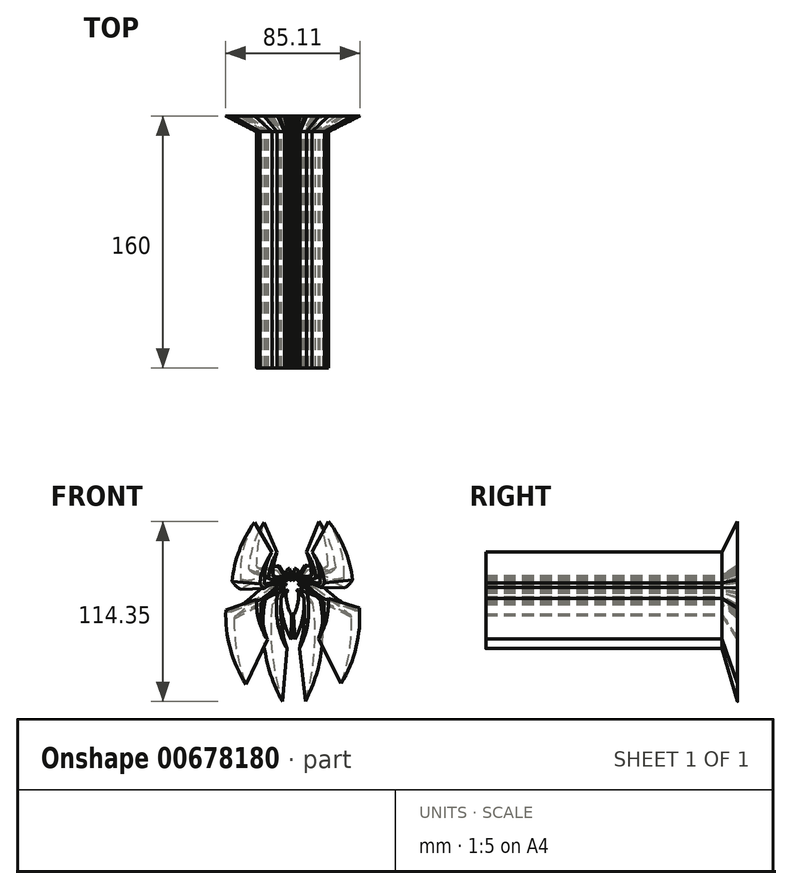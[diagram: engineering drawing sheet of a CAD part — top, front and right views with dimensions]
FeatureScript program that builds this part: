
annotation { "Feature Type Name" : "Feature", "Feature Type Description" : "" }
export const myFeature = defineFeature(function(context is Context, id is Id, definition is map)
    precondition{}
    {
        {
            var Q0;
            Q0=qCreatedBy(makeId("Front.planeOp"),FACE);
            var sketch = newSketch(context, id + "F0", { "sketchPlane" : qUnion([Q0])});
            skArc(sketch, "E0", {"start": v(-12.95, 21.82) * mm, "mid": v(-18.14, 12.28) * mm, "end": v(-20.61, 1.7) * mm});
            skArc(sketch, "E1", {"start": v(-7.35, 2.72) * mm, "mid": v(-12.76, 1.42) * mm, "end": v(-17.74, -1.05) * mm});
            skLineSegment(sketch, "E2", {"start": v(-7.35, 2.72) * mm, "end": v(-4.17, 1.94) * mm});
            skLineSegment(sketch, "E3", {"start": v(-4.17, 0.92) * mm, "end": v(-8.94, 0.99) * mm});
            skLineSegment(sketch, "E4", {"start": v(-20.96, -8.77) * mm, "end": v(-22.05, -8.77) * mm});
            skLineSegment(sketch, "E5", {"start": v(-22.05, -8.77) * mm, "end": v(-22.72, -8.06) * mm});
            skArc(sketch, "E6", {"start": v(-22.72, -8.06) * mm, "mid": v(-21.2, -21.34) * mm, "end": v(-15.81, -33.57) * mm});
            skArc(sketch, "E7", {"start": v(-19.94, -11.2) * mm, "mid": v(-18.92, -22.58) * mm, "end": v(-15.81, -33.57) * mm});
            skArc(sketch, "E8", {"start": v(-9.25, -4.09) * mm, "mid": v(-6.79, -2.87) * mm, "end": v(-5, -0.78) * mm});
            skArc(sketch, "E9", {"start": v(-9.25, -4.09) * mm, "mid": v(-9.38, -22.21) * mm, "end": v(-3.45, -39.34) * mm});
            skArc(sketch, "E10", {"start": v(-6.96, -6.37) * mm, "mid": v(-6.9, -23.04) * mm, "end": v(-3.45, -39.34) * mm});
            skArc(sketch, "E11", {"start": v(-3.45, -2.1) * mm, "mid": v(-5.56, -3.95) * mm, "end": v(-6.96, -6.37) * mm});
            skArc(sketch, "E12", {"start": v(-2.87, -2.74) * mm, "mid": v(-3.03, -2.3) * mm, "end": v(-3.45, -2.1) * mm});
            skArc(sketch, "E13", {"start": v(-2.87, -2.74) * mm, "mid": v(-3.6, -3.27) * mm, "end": v(-3.96, -4.09) * mm});
            skArc(sketch, "E14", {"start": v(-3.96, -4.09) * mm, "mid": v(-3.09, -11.38) * mm, "end": v(-0.42, -18.22) * mm});
            skArc(sketch, "E15", {"start": v(0.24, -17.46) * mm, "mid": v(-0.3, -17.65) * mm, "end": v(-0.42, -18.22) * mm});
            skArc(sketch, "E16", {"start": v(-4.17, 0.92) * mm, "mid": v(-3.96, 1.43) * mm, "end": v(-4.17, 1.94) * mm});
            skArc(sketch, "E17", {"start": v(-20.96, -8.77) * mm, "mid": v(-14.65, -4.26) * mm, "end": v(-8.94, 0.99) * mm});
            skArc(sketch, "E18", {"start": v(-5, -0.78) * mm, "mid": v(-6.44, -0.47) * mm, "end": v(-7.87, -0.78) * mm});
            skArc(sketch, "E19", {"start": v(-19.36, -10.12) * mm, "mid": v(-13.61, -5.46) * mm, "end": v(-7.87, -0.78) * mm});
            skArc(sketch, "E20", {"start": v(-19.36, -10.12) * mm, "mid": v(-19.82, -10.57) * mm, "end": v(-19.94, -11.2) * mm});
            skArc(sketch, "E21", {"start": v(-20.61, 1.7) * mm, "mid": v(-19.32, 0.17) * mm, "end": v(-17.74, -1.05) * mm});
            skArc(sketch, "E22", {"start": v(-12.95, 21.82) * mm, "mid": v(-16.8, 12.49) * mm, "end": v(-17.74, 2.44) * mm});
            skArc(sketch, "E23", {"start": v(-17.74, 2.44) * mm, "mid": v(-17.57, 1.78) * mm, "end": v(-16.9, 1.7) * mm});
            skArc(sketch, "E24", {"start": v(-16.9, 1.7) * mm, "mid": v(-12.62, 2.7) * mm, "end": v(-8.54, 4.31) * mm});
            skArc(sketch, "E25", {"start": v(-6.8, 4.31) * mm, "mid": v(-7.67, 4.47) * mm, "end": v(-8.54, 4.31) * mm});
            skArc(sketch, "E26", {"start": v(-6.8, 4.31) * mm, "mid": v(-5.62, 3.5) * mm, "end": v(-4.33, 2.85) * mm});
            skArc(sketch, "E27", {"start": v(-4.33, 2.85) * mm, "mid": v(-3.97, 2.98) * mm, "end": v(-3.9, 3.36) * mm});
            skArc(sketch, "E28", {"start": v(-3.9, 3.36) * mm, "mid": v(-4.45, 4.49) * mm, "end": v(-5.37, 5.34) * mm});
            skArc(sketch, "E29", {"start": v(-5.37, 5.34) * mm, "mid": v(-8.87, 5.53) * mm, "end": v(-12.34, 5.02) * mm});
            skArc(sketch, "E30", {"start": v(-12.96, 4.31) * mm, "mid": v(-12.61, 4.63) * mm, "end": v(-12.34, 5.02) * mm});
            skArc(sketch, "E31", {"start": v(-15, 5.99) * mm, "mid": v(-14.07, 5.04) * mm, "end": v(-12.96, 4.31) * mm});
            skArc(sketch, "E32", {"start": v(-9.71, 21.82) * mm, "mid": v(-13.3, 14.22) * mm, "end": v(-15, 5.99) * mm});
            skArc(sketch, "E33", {"start": v(-9.71, 21.82) * mm, "mid": v(-11.7, 14.5) * mm, "end": v(-12.34, 6.95) * mm});
            skArc(sketch, "E34", {"start": v(-12.34, 6.95) * mm, "mid": v(-12.26, 6.64) * mm, "end": v(-12.02, 6.43) * mm});
            skArc(sketch, "E35", {"start": v(-12.02, 6.43) * mm, "mid": v(-8.49, 6.3) * mm, "end": v(-5.02, 6.95) * mm});
            skArc(sketch, "E36", {"start": v(-4.51, 6.95) * mm, "mid": v(-4.76, 7.03) * mm, "end": v(-5.02, 6.95) * mm});
            skArc(sketch, "E37", {"start": v(-4.51, 6.95) * mm, "mid": v(-3.87, 5.55) * mm, "end": v(-2.67, 4.6) * mm});
            skArc(sketch, "E38", {"start": v(-2.67, 4.6) * mm, "mid": v(-2.4, 4.75) * mm, "end": v(-2.22, 5) * mm});
            skArc(sketch, "E39", {"start": v(-0.95, 6.13) * mm, "mid": v(-1.72, 5.7) * mm, "end": v(-2.22, 5) * mm});
            skArc(sketch, "E40", {"start": v(-1.4, 5) * mm, "mid": v(-1.1, 5.53) * mm, "end": v(-0.95, 6.13) * mm});
            skArc(sketch, "E41", {"start": v(-1.4, 5) * mm, "mid": v(-1.52, 4.91) * mm, "end": v(-1.56, 4.78) * mm});
            skArc(sketch, "E42", {"start": v(-1.56, 4.78) * mm, "mid": v(-1.55, 4.46) * mm, "end": v(-1.4, 4.18) * mm});
            skArc(sketch, "E43", {"start": v(-1.4, 4.18) * mm, "mid": v(-1.14, 4.04) * mm, "end": v(-0.87, 4.18) * mm});
            skArc(sketch, "E44", {"start": v(-0.4, 5) * mm, "mid": v(-0.75, 4.65) * mm, "end": v(-0.87, 4.18) * mm});
            skArc(sketch, "E45", {"start": v(0, 4.18) * mm, "mid": v(-0.11, 4.63) * mm, "end": v(-0.4, 5) * mm});
            skArc(sketch, "E46", {"start": v(0, 4.18) * mm, "mid": v(0.17, 4.06) * mm, "end": v(0.36, 3.98) * mm});
            skArc(sketch, "E47.MirrorCS", {"start": v(9.35, -3.85) * mm, "mid": v(9.94, -21.96) * mm, "end": v(4.46, -39.24) * mm});
            skArc(sketch, "E48.MirrorCS", {"start": v(7.12, -6.2) * mm, "mid": v(7.48, -22.85) * mm, "end": v(4.46, -39.24) * mm});
            skArc(sketch, "E49.MirrorCS", {"start": v(0.2, -17.46) * mm, "mid": v(0.76, -17.63) * mm, "end": v(0.88, -18.2) * mm});
            skArc(sketch, "E50.MirrorCS", {"start": v(4.07, -3.99) * mm, "mid": v(3.38, -11.3) * mm, "end": v(0.88, -18.2) * mm});
            skArc(sketch, "E51.MirrorCS", {"start": v(2.94, -2.67) * mm, "mid": v(3.68, -3.17) * mm, "end": v(4.07, -3.99) * mm});
            skArc(sketch, "E52.MirrorCS", {"start": v(2.94, -2.67) * mm, "mid": v(3.1, -2.22) * mm, "end": v(3.5, -2) * mm});
            skArc(sketch, "E53.MirrorCS", {"start": v(3.5, -2) * mm, "mid": v(5.66, -3.8) * mm, "end": v(7.12, -6.2) * mm});
            skArc(sketch, "E54.MirrorCS", {"start": v(9.35, -3.85) * mm, "mid": v(6.86, -2.7) * mm, "end": v(5.03, -0.66) * mm});
            skArc(sketch, "E55.MirrorCS", {"start": v(5.03, -0.66) * mm, "mid": v(6.45, -0.3) * mm, "end": v(7.89, -0.58) * mm});
            skArc(sketch, "E56.MirrorCS", {"start": v(19.6, -9.62) * mm, "mid": v(13.75, -5.1) * mm, "end": v(7.89, -0.58) * mm});
            skArc(sketch, "E57.MirrorCS", {"start": v(21.17, -8.23) * mm, "mid": v(14.75, -3.88) * mm, "end": v(8.91, 1.22) * mm});
            skArc(sketch, "E58.MirrorCS", {"start": v(22.92, -7.48) * mm, "mid": v(21.75, -20.79) * mm, "end": v(16.67, -33.15) * mm});
            skArc(sketch, "E59.MirrorCS", {"start": v(20.22, -10.7) * mm, "mid": v(19.5, -22.09) * mm, "end": v(16.67, -33.15) * mm});
            skArc(sketch, "E60.MirrorCS", {"start": v(19.6, -9.62) * mm, "mid": v(20.09, -10.06) * mm, "end": v(20.22, -10.7) * mm});
            skLineSegment(sketch, "E61.MirrorCS", {"start": v(21.17, -8.23) * mm, "end": v(22.27, -8.2) * mm});
            skLineSegment(sketch, "E62.MirrorCS", {"start": v(22.27, -8.2) * mm, "end": v(22.92, -7.48) * mm});
            skLineSegment(sketch, "E63.MirrorCS", {"start": v(4.14, 1.02) * mm, "end": v(8.91, 1.22) * mm});
            skArc(sketch, "E64.MirrorCS", {"start": v(4.14, 1.02) * mm, "mid": v(3.92, 1.53) * mm, "end": v(4.12, 2.05) * mm});
            skLineSegment(sketch, "E65.MirrorCS", {"start": v(7.28, 2.9) * mm, "end": v(4.12, 2.05) * mm});
            skArc(sketch, "E66.MirrorCS", {"start": v(7.28, 2.9) * mm, "mid": v(12.72, 1.75) * mm, "end": v(17.76, -0.6) * mm});
            skArc(sketch, "E67.MirrorCS", {"start": v(16.85, 2.14) * mm, "mid": v(12.55, 3.01) * mm, "end": v(8.43, 4.53) * mm});
            skArc(sketch, "E68.MirrorCS", {"start": v(6.7, 4.49) * mm, "mid": v(7.56, 4.67) * mm, "end": v(8.43, 4.53) * mm});
            skArc(sketch, "E69.MirrorCS", {"start": v(6.7, 4.49) * mm, "mid": v(5.53, 3.64) * mm, "end": v(4.26, 2.96) * mm});
            skArc(sketch, "E70.MirrorCS", {"start": v(4.26, 2.96) * mm, "mid": v(3.9, 3.08) * mm, "end": v(3.8, 3.46) * mm});
            skArc(sketch, "E71.MirrorCS", {"start": v(20.56, 2.23) * mm, "mid": v(19.31, 0.67) * mm, "end": v(17.76, -0.6) * mm});
            skArc(sketch, "E72.MirrorCS", {"start": v(12.38, 22.15) * mm, "mid": v(17.82, 12.74) * mm, "end": v(20.56, 2.23) * mm});
            skArc(sketch, "E73.MirrorCS", {"start": v(12.38, 22.15) * mm, "mid": v(16.47, 12.91) * mm, "end": v(17.67, 2.89) * mm});
            skArc(sketch, "E74.MirrorCS", {"start": v(14.84, 6.37) * mm, "mid": v(13.94, 5.4) * mm, "end": v(12.85, 4.64) * mm});
            skArc(sketch, "E75.MirrorCS", {"start": v(5.23, 5.48) * mm, "mid": v(8.73, 5.75) * mm, "end": v(12.2, 5.34) * mm});
            skArc(sketch, "E76.MirrorCS", {"start": v(12.85, 4.64) * mm, "mid": v(12.49, 4.95) * mm, "end": v(12.2, 5.34) * mm});
            skArc(sketch, "E77.MirrorCS", {"start": v(3.8, 3.46) * mm, "mid": v(4.34, 4.6) * mm, "end": v(5.23, 5.48) * mm});
            skArc(sketch, "E78.MirrorCS", {"start": v(11.85, 6.73) * mm, "mid": v(8.32, 6.5) * mm, "end": v(4.84, 7.08) * mm});
            skArc(sketch, "E79.MirrorCS", {"start": v(4.33, 7.06) * mm, "mid": v(4.58, 7.15) * mm, "end": v(4.84, 7.08) * mm});
            skArc(sketch, "E80.MirrorCS", {"start": v(9.15, 22.06) * mm, "mid": v(11.32, 14.8) * mm, "end": v(12.16, 7.26) * mm});
            skArc(sketch, "E81.MirrorCS", {"start": v(9.15, 22.06) * mm, "mid": v(12.93, 14.56) * mm, "end": v(14.84, 6.37) * mm});
            skArc(sketch, "E82.MirrorCS", {"start": v(4.33, 7.06) * mm, "mid": v(3.72, 5.65) * mm, "end": v(2.55, 4.66) * mm});
            skArc(sketch, "E83.MirrorCS", {"start": v(0.79, 6.15) * mm, "mid": v(1.57, 5.75) * mm, "end": v(2.1, 5.05) * mm});
            skArc(sketch, "E84.MirrorCS", {"start": v(1.28, 5.03) * mm, "mid": v(0.96, 5.55) * mm, "end": v(0.79, 6.15) * mm});
            skArc(sketch, "E85.MirrorCS", {"start": v(0.27, 5) * mm, "mid": v(0.63, 4.67) * mm, "end": v(0.76, 4.2) * mm});
            skArc(sketch, "E86.MirrorCS", {"start": v(-0.1, 4.18) * mm, "mid": v(0, 4.63) * mm, "end": v(0.27, 5) * mm});
            skArc(sketch, "E87.MirrorCS", {"start": v(-0.1, 4.18) * mm, "mid": v(-0.27, 4.05) * mm, "end": v(-0.46, 3.97) * mm});
            skArc(sketch, "E88.MirrorCS", {"start": v(1.3, 4.21) * mm, "mid": v(1.04, 4.07) * mm, "end": v(0.76, 4.2) * mm});
            skArc(sketch, "E89.MirrorCS", {"start": v(2.55, 4.66) * mm, "mid": v(2.28, 4.8) * mm, "end": v(2.1, 5.05) * mm});
            skArc(sketch, "E90.MirrorCS", {"start": v(1.28, 5.03) * mm, "mid": v(1.4, 4.95) * mm, "end": v(1.44, 4.82) * mm});
            skArc(sketch, "E91.MirrorCS", {"start": v(1.44, 4.82) * mm, "mid": v(1.43, 4.5) * mm, "end": v(1.3, 4.21) * mm});
            skArc(sketch, "E92.MirrorCS", {"start": v(12.16, 7.26) * mm, "mid": v(12.08, 6.95) * mm, "end": v(11.85, 6.73) * mm});
            skArc(sketch, "E93.MirrorCS", {"start": v(17.67, 2.89) * mm, "mid": v(17.52, 2.23) * mm, "end": v(16.85, 2.14) * mm});
            skSolve(sketch);
        }
        {
            var Q0;
            Q0=makeQuery(id+"F0.imprint","IMPRINT",FACE,{"disambiguationData":[TD([[makeQuery(id+"F0.imprint","IMPRINT",EDGE,{"derivedFrom":sQuery(id+"F0.wireOp",EDGE,"E0")}),1.0]])]});
            var Q1;
            Q1=sQuery(id+"F0.wireOp",EDGE,"E0");
            var Q2;
            Q2=sQuery(id+"F0.wireOp",EDGE,"E1");
            var Q3;
            Q3=sQuery(id+"F0.wireOp",EDGE,"E2");
            var Q4;
            Q4=sQuery(id+"F0.wireOp",EDGE,"E3");
            var Q5;
            Q5=sQuery(id+"F0.wireOp",EDGE,"E4");
            var Q6;
            Q6=sQuery(id+"F0.wireOp",EDGE,"E5");
            var Q7;
            Q7=sQuery(id+"F0.wireOp",EDGE,"E6");
            var Q8;
            Q8=sQuery(id+"F0.wireOp",EDGE,"E7");
            var Q9;
            Q9=sQuery(id+"F0.wireOp",EDGE,"E8");
            var Q10;
            Q10=sQuery(id+"F0.wireOp",EDGE,"E9");
            var Q11;
            Q11=sQuery(id+"F0.wireOp",EDGE,"E10");
            var Q12;
            Q12=sQuery(id+"F0.wireOp",EDGE,"E11");
            var Q13;
            Q13=sQuery(id+"F0.wireOp",EDGE,"E12");
            var Q14;
            Q14=sQuery(id+"F0.wireOp",EDGE,"E13");
            var Q15;
            Q15=sQuery(id+"F0.wireOp",EDGE,"E14");
            var Q16;
            Q16=sQuery(id+"F0.wireOp",EDGE,"E15");
            var Q17;
            Q17=sQuery(id+"F0.wireOp",EDGE,"E16");
            var Q18;
            Q18=sQuery(id+"F0.wireOp",EDGE,"E17");
            var Q19;
            Q19=sQuery(id+"F0.wireOp",EDGE,"E18");
            var Q20;
            Q20=sQuery(id+"F0.wireOp",EDGE,"E19");
            var Q21;
            Q21=sQuery(id+"F0.wireOp",EDGE,"E20");
            var Q22;
            Q22=sQuery(id+"F0.wireOp",EDGE,"E21");
            var Q23;
            Q23=sQuery(id+"F0.wireOp",EDGE,"E22");
            var Q24;
            Q24=sQuery(id+"F0.wireOp",EDGE,"E23");
            var Q25;
            Q25=sQuery(id+"F0.wireOp",EDGE,"E24");
            var Q26;
            Q26=sQuery(id+"F0.wireOp",EDGE,"E25");
            var Q27;
            Q27=sQuery(id+"F0.wireOp",EDGE,"E26");
            var Q28;
            Q28=sQuery(id+"F0.wireOp",EDGE,"E27");
            var Q29;
            Q29=sQuery(id+"F0.wireOp",EDGE,"E28");
            var Q30;
            Q30=sQuery(id+"F0.wireOp",EDGE,"E29");
            var Q31;
            Q31=sQuery(id+"F0.wireOp",EDGE,"E30");
            var Q32;
            Q32=sQuery(id+"F0.wireOp",EDGE,"E31");
            var Q33;
            Q33=sQuery(id+"F0.wireOp",EDGE,"E32");
            var Q34;
            Q34=sQuery(id+"F0.wireOp",EDGE,"E33");
            var Q35;
            Q35=sQuery(id+"F0.wireOp",EDGE,"E34");
            var Q36;
            Q36=sQuery(id+"F0.wireOp",EDGE,"E35");
            var Q37;
            Q37=sQuery(id+"F0.wireOp",EDGE,"E36");
            var Q38;
            Q38=sQuery(id+"F0.wireOp",EDGE,"E37");
            var Q39;
            Q39=sQuery(id+"F0.wireOp",EDGE,"E38");
            var Q40;
            Q40=sQuery(id+"F0.wireOp",EDGE,"E39");
            var Q41;
            Q41=sQuery(id+"F0.wireOp",EDGE,"E40");
            var Q42;
            Q42=sQuery(id+"F0.wireOp",EDGE,"E41");
            var Q43;
            Q43=sQuery(id+"F0.wireOp",EDGE,"E42");
            var Q44;
            Q44=sQuery(id+"F0.wireOp",EDGE,"E43");
            var Q45;
            Q45=sQuery(id+"F0.wireOp",EDGE,"E44");
            var Q46;
            Q46=sQuery(id+"F0.wireOp",EDGE,"E45");
            var Q47;
            Q47=sQuery(id+"F0.wireOp",EDGE,"E46");
            var Q48;
            Q48=sQuery(id+"F0.wireOp",EDGE,"E47.MirrorCS");
            var Q49;
            Q49=sQuery(id+"F0.wireOp",EDGE,"E48.MirrorCS");
            var Q50;
            Q50=sQuery(id+"F0.wireOp",EDGE,"E49.MirrorCS");
            var Q51;
            Q51=sQuery(id+"F0.wireOp",EDGE,"E50.MirrorCS");
            var Q52;
            Q52=sQuery(id+"F0.wireOp",EDGE,"E51.MirrorCS");
            var Q53;
            Q53=sQuery(id+"F0.wireOp",EDGE,"E52.MirrorCS");
            var Q54;
            Q54=sQuery(id+"F0.wireOp",EDGE,"E53.MirrorCS");
            var Q55;
            Q55=sQuery(id+"F0.wireOp",EDGE,"E54.MirrorCS");
            var Q56;
            Q56=sQuery(id+"F0.wireOp",EDGE,"E55.MirrorCS");
            var Q57;
            Q57=sQuery(id+"F0.wireOp",EDGE,"E56.MirrorCS");
            var Q58;
            Q58=sQuery(id+"F0.wireOp",EDGE,"E57.MirrorCS");
            var Q59;
            Q59=sQuery(id+"F0.wireOp",EDGE,"E58.MirrorCS");
            var Q60;
            Q60=sQuery(id+"F0.wireOp",EDGE,"E59.MirrorCS");
            var Q61;
            Q61=sQuery(id+"F0.wireOp",EDGE,"E60.MirrorCS");
            var Q62;
            Q62=sQuery(id+"F0.wireOp",EDGE,"E61.MirrorCS");
            var Q63;
            Q63=sQuery(id+"F0.wireOp",EDGE,"E62.MirrorCS");
            var Q64;
            Q64=sQuery(id+"F0.wireOp",EDGE,"E63.MirrorCS");
            var Q65;
            Q65=sQuery(id+"F0.wireOp",EDGE,"E64.MirrorCS");
            var Q66;
            Q66=sQuery(id+"F0.wireOp",EDGE,"E65.MirrorCS");
            var Q67;
            Q67=sQuery(id+"F0.wireOp",EDGE,"E66.MirrorCS");
            var Q68;
            Q68=sQuery(id+"F0.wireOp",EDGE,"E67.MirrorCS");
            var Q69;
            Q69=sQuery(id+"F0.wireOp",EDGE,"E68.MirrorCS");
            var Q70;
            Q70=sQuery(id+"F0.wireOp",EDGE,"E69.MirrorCS");
            var Q71;
            Q71=sQuery(id+"F0.wireOp",EDGE,"E70.MirrorCS");
            var Q72;
            Q72=sQuery(id+"F0.wireOp",EDGE,"E71.MirrorCS");
            var Q73;
            Q73=sQuery(id+"F0.wireOp",EDGE,"E72.MirrorCS");
            var Q74;
            Q74=sQuery(id+"F0.wireOp",EDGE,"E73.MirrorCS");
            var Q75;
            Q75=sQuery(id+"F0.wireOp",EDGE,"E74.MirrorCS");
            var Q76;
            Q76=sQuery(id+"F0.wireOp",EDGE,"E75.MirrorCS");
            var Q77;
            Q77=sQuery(id+"F0.wireOp",EDGE,"E76.MirrorCS");
            var Q78;
            Q78=sQuery(id+"F0.wireOp",EDGE,"E77.MirrorCS");
            var Q79;
            Q79=sQuery(id+"F0.wireOp",EDGE,"E78.MirrorCS");
            var Q80;
            Q80=sQuery(id+"F0.wireOp",EDGE,"E79.MirrorCS");
            var Q81;
            Q81=sQuery(id+"F0.wireOp",EDGE,"E80.MirrorCS");
            var Q82;
            Q82=sQuery(id+"F0.wireOp",EDGE,"E81.MirrorCS");
            var Q83;
            Q83=sQuery(id+"F0.wireOp",EDGE,"E82.MirrorCS");
            var Q84;
            Q84=sQuery(id+"F0.wireOp",EDGE,"E83.MirrorCS");
            var Q85;
            Q85=sQuery(id+"F0.wireOp",EDGE,"E84.MirrorCS");
            var Q86;
            Q86=sQuery(id+"F0.wireOp",EDGE,"E85.MirrorCS");
            var Q87;
            Q87=sQuery(id+"F0.wireOp",EDGE,"E86.MirrorCS");
            var Q88;
            Q88=sQuery(id+"F0.wireOp",EDGE,"E87.MirrorCS");
            var Q89;
            Q89=sQuery(id+"F0.wireOp",EDGE,"E88.MirrorCS");
            var Q90;
            Q90=sQuery(id+"F0.wireOp",EDGE,"E89.MirrorCS");
            var Q91;
            Q91=sQuery(id+"F0.wireOp",EDGE,"E90.MirrorCS");
            var Q92;
            Q92=sQuery(id+"F0.wireOp",EDGE,"E91.MirrorCS");
            var Q93;
            Q93=sQuery(id+"F0.wireOp",EDGE,"E92.MirrorCS");
            var Q94;
            Q94=sQuery(id+"F0.wireOp",EDGE,"E93.MirrorCS");
            extrude(context, id + "F1", {"entities" : qUnion([Q0]), "surfaceEntities" : qUnion([Q1, Q2, Q3, Q4, Q5, Q6, Q7, Q8, Q9, Q10, Q11, Q12, Q13, Q14, Q15, Q16, Q17, Q18, Q19, Q20, Q21, Q22, Q23, Q24, Q25, Q26, Q27, Q28, Q29, Q30, Q31, Q32, Q33, Q34, Q35, Q36, Q37, Q38, Q39, Q40, Q41, Q42, Q43, Q44, Q45, Q46, Q47, Q48, Q49, Q50, Q51, Q52, Q53, Q54, Q55, Q56, Q57, Q58, Q59, Q60, Q61, Q62, Q63, Q64, Q65, Q66, Q67, Q68, Q69, Q70, Q71, Q72, Q73, Q74, Q75, Q76, Q77, Q78, Q79, Q80, Q81, Q82, Q83, Q84, Q85, Q86, Q87, Q88, Q89, Q90, Q91, Q92, Q93, Q94]), "depth" : 150 * mm, "offsetDistance" : 25 * mm});
        }
        {
            var Q0;
            Q0=qCreatedBy(makeId("Front.planeOp"),FACE);
            cPlane(context, id + "F2", {"entities" : qUnion([Q0]), "cplaneType" : CPlaneType.OFFSET, "offset" : 10 * mm, "oppositeDirection" : true, "width" : 150 * mm, "height" : 150 * mm});
        }
        {
            var Q0;
            Q0=qCreatedBy(id+"F2.planeOp",FACE);
            var sketch = newSketch(context, id + "F3", { "sketchPlane" : qUnion([Q0])});
            skArc(sketch, "E94", {"start": v(-24, 40.8) * mm, "mid": v(-33.66, 23.06) * mm, "end": v(-38.26, 3.39) * mm});
            skArc(sketch, "E95", {"start": v(-13.59, 5.28) * mm, "mid": v(-23.65, 2.87) * mm, "end": v(-32.91, -1.73) * mm});
            skLineSegment(sketch, "E96", {"start": v(-13.59, 5.28) * mm, "end": v(-7.67, 3.83) * mm});
            skLineSegment(sketch, "E97", {"start": v(-7.67, 1.92) * mm, "end": v(-16.55, 2.05) * mm});
            skLineSegment(sketch, "E98", {"start": v(-38.9, -16.09) * mm, "end": v(-40.93, -16.09) * mm});
            skLineSegment(sketch, "E99", {"start": v(-40.93, -16.09) * mm, "end": v(-42.18, -14.77) * mm});
            skArc(sketch, "E100", {"start": v(-42.18, -14.77) * mm, "mid": v(-39.36, -39.47) * mm, "end": v(-29.33, -62.2) * mm});
            skArc(sketch, "E101", {"start": v(-37, -20.62) * mm, "mid": v(-35.11, -41.77) * mm, "end": v(-29.33, -62.2) * mm});
            skArc(sketch, "E102", {"start": v(-17.12, -7.38) * mm, "mid": v(-12.55, -5.12) * mm, "end": v(-9.24, -1.24) * mm});
            skArc(sketch, "E103", {"start": v(-17.12, -7.38) * mm, "mid": v(-17.36, -41.09) * mm, "end": v(-6.34, -72.94) * mm});
            skArc(sketch, "E104", {"start": v(-12.86, -11.63) * mm, "mid": v(-12.74, -42.62) * mm, "end": v(-6.34, -72.94) * mm});
            skArc(sketch, "E105", {"start": v(-6.34, -3.68) * mm, "mid": v(-10.26, -7.12) * mm, "end": v(-12.86, -11.63) * mm});
            skArc(sketch, "E106", {"start": v(-5.25, -4.88) * mm, "mid": v(-5.56, -4.06) * mm, "end": v(-6.34, -3.68) * mm});
            skArc(sketch, "E107", {"start": v(-5.25, -4.88) * mm, "mid": v(-6.61, -5.86) * mm, "end": v(-7.3, -7.38) * mm});
            skArc(sketch, "E108", {"start": v(-7.3, -7.38) * mm, "mid": v(-5.66, -20.94) * mm, "end": v(-0.7, -33.66) * mm});
            skArc(sketch, "E109", {"start": v(0.53, -32.25) * mm, "mid": v(-0.5, -32.6) * mm, "end": v(-0.7, -33.66) * mm});
            skArc(sketch, "E110", {"start": v(-7.67, 1.92) * mm, "mid": v(-7.28, 2.88) * mm, "end": v(-7.67, 3.83) * mm});
            skArc(sketch, "E111", {"start": v(-38.9, -16.09) * mm, "mid": v(-27.16, -7.7) * mm, "end": v(-16.55, 2.05) * mm});
            skArc(sketch, "E112", {"start": v(-9.24, -1.24) * mm, "mid": v(-11.9, -0.65) * mm, "end": v(-14.56, -1.24) * mm});
            skArc(sketch, "E113", {"start": v(-35.92, -18.6) * mm, "mid": v(-25.24, -9.93) * mm, "end": v(-14.56, -1.24) * mm});
            skArc(sketch, "E114", {"start": v(-35.92, -18.6) * mm, "mid": v(-36.79, -19.44) * mm, "end": v(-37, -20.62) * mm});
            skArc(sketch, "E115", {"start": v(-38.26, 3.39) * mm, "mid": v(-35.86, 0.54) * mm, "end": v(-32.91, -1.73) * mm});
            skArc(sketch, "E116", {"start": v(-24, 40.8) * mm, "mid": v(-31.16, 23.44) * mm, "end": v(-32.91, 4.75) * mm});
            skArc(sketch, "E117", {"start": v(-32.91, 4.75) * mm, "mid": v(-32.6, 3.53) * mm, "end": v(-31.35, 3.39) * mm});
            skArc(sketch, "E118", {"start": v(-31.35, 3.39) * mm, "mid": v(-23.4, 5.23) * mm, "end": v(-15.8, 8.24) * mm});
            skArc(sketch, "E119", {"start": v(-12.58, 8.24) * mm, "mid": v(-14.2, 8.53) * mm, "end": v(-15.8, 8.24) * mm});
            skArc(sketch, "E120", {"start": v(-12.58, 8.24) * mm, "mid": v(-10.38, 6.72) * mm, "end": v(-7.98, 5.52) * mm});
            skArc(sketch, "E121", {"start": v(-7.98, 5.52) * mm, "mid": v(-7.31, 5.77) * mm, "end": v(-7.17, 6.46) * mm});
            skArc(sketch, "E122", {"start": v(-7.17, 6.46) * mm, "mid": v(-8.2, 8.56) * mm, "end": v(-9.91, 10.16) * mm});
            skArc(sketch, "E123", {"start": v(-9.91, 10.16) * mm, "mid": v(-16.42, 10.5) * mm, "end": v(-22.87, 9.56) * mm});
            skArc(sketch, "E124", {"start": v(-24.03, 8.24) * mm, "mid": v(-23.38, 8.84) * mm, "end": v(-22.87, 9.56) * mm});
            skArc(sketch, "E125", {"start": v(-27.82, 11.36) * mm, "mid": v(-26.1, 9.6) * mm, "end": v(-24.03, 8.24) * mm});
            skArc(sketch, "E126", {"start": v(-17.99, 40.8) * mm, "mid": v(-24.66, 26.67) * mm, "end": v(-27.82, 11.36) * mm});
            skArc(sketch, "E127", {"start": v(-17.99, 40.8) * mm, "mid": v(-21.67, 27.2) * mm, "end": v(-22.87, 13.14) * mm});
            skArc(sketch, "E128", {"start": v(-22.87, 13.14) * mm, "mid": v(-22.72, 12.57) * mm, "end": v(-22.27, 12.18) * mm});
            skArc(sketch, "E129", {"start": v(-22.27, 12.18) * mm, "mid": v(-15.7, 11.92) * mm, "end": v(-9.25, 13.14) * mm});
            skArc(sketch, "E130", {"start": v(-8.31, 13.14) * mm, "mid": v(-8.78, 13.3) * mm, "end": v(-9.25, 13.14) * mm});
            skArc(sketch, "E131", {"start": v(-8.31, 13.14) * mm, "mid": v(-7.12, 10.55) * mm, "end": v(-4.89, 8.76) * mm});
            skArc(sketch, "E132", {"start": v(-4.89, 8.76) * mm, "mid": v(-4.4, 9.05) * mm, "end": v(-4.06, 9.5) * mm});
            skArc(sketch, "E133", {"start": v(-1.68, 11.61) * mm, "mid": v(-3.12, 10.84) * mm, "end": v(-4.06, 9.5) * mm});
            skArc(sketch, "E134", {"start": v(-2.54, 9.5) * mm, "mid": v(-1.97, 10.5) * mm, "end": v(-1.68, 11.61) * mm});
            skArc(sketch, "E135", {"start": v(-2.54, 9.5) * mm, "mid": v(-2.75, 9.35) * mm, "end": v(-2.83, 9.11) * mm});
            skArc(sketch, "E136", {"start": v(-2.83, 9.11) * mm, "mid": v(-2.8, 8.52) * mm, "end": v(-2.54, 7.99) * mm});
            skArc(sketch, "E137", {"start": v(-2.54, 7.99) * mm, "mid": v(-2.04, 7.74) * mm, "end": v(-1.54, 7.99) * mm});
            skArc(sketch, "E138", {"start": v(-0.67, 9.5) * mm, "mid": v(-1.31, 8.86) * mm, "end": v(-1.54, 7.99) * mm});
            skArc(sketch, "E139", {"start": v(0.08, 7.99) * mm, "mid": v(-0.13, 8.83) * mm, "end": v(-0.67, 9.5) * mm});
            skArc(sketch, "E140", {"start": v(0.08, 7.99) * mm, "mid": v(0.39, 7.77) * mm, "end": v(0.74, 7.62) * mm});
            skArc(sketch, "E141.MirrorCS", {"start": v(17.47, -6.94) * mm, "mid": v(18.57, -40.63) * mm, "end": v(8.37, -72.75) * mm});
            skArc(sketch, "E142.MirrorCS", {"start": v(13.31, -11.3) * mm, "mid": v(13.98, -42.28) * mm, "end": v(8.37, -72.75) * mm});
            skArc(sketch, "E143.MirrorCS", {"start": v(0.45, -32.25) * mm, "mid": v(1.49, -32.57) * mm, "end": v(1.72, -33.63) * mm});
            skArc(sketch, "E144.MirrorCS", {"start": v(7.64, -7.2) * mm, "mid": v(6.36, -20.79) * mm, "end": v(1.72, -33.63) * mm});
            skArc(sketch, "E145.MirrorCS", {"start": v(5.54, -4.74) * mm, "mid": v(6.92, -5.68) * mm, "end": v(7.64, -7.2) * mm});
            skArc(sketch, "E146.MirrorCS", {"start": v(5.54, -4.74) * mm, "mid": v(5.82, -3.92) * mm, "end": v(6.6, -3.51) * mm});
            skArc(sketch, "E147.MirrorCS", {"start": v(6.6, -3.51) * mm, "mid": v(10.6, -6.85) * mm, "end": v(13.31, -11.3) * mm});
            skArc(sketch, "E148.MirrorCS", {"start": v(17.47, -6.94) * mm, "mid": v(12.84, -4.8) * mm, "end": v(9.43, -1) * mm});
            skArc(sketch, "E149.MirrorCS", {"start": v(9.43, -1) * mm, "mid": v(12.07, -0.34) * mm, "end": v(14.75, -0.86) * mm});
            skArc(sketch, "E150.MirrorCS", {"start": v(36.55, -17.67) * mm, "mid": v(25.64, -9.27) * mm, "end": v(14.75, -0.86) * mm});
            skArc(sketch, "E151.MirrorCS", {"start": v(39.45, -15.08) * mm, "mid": v(27.51, -7) * mm, "end": v(16.65, 2.48) * mm});
            skArc(sketch, "E152.MirrorCS", {"start": v(42.7, -13.69) * mm, "mid": v(40.52, -38.44) * mm, "end": v(31.07, -61.43) * mm});
            skArc(sketch, "E153.MirrorCS", {"start": v(37.68, -19.66) * mm, "mid": v(36.33, -40.86) * mm, "end": v(31.07, -61.43) * mm});
            skArc(sketch, "E154.MirrorCS", {"start": v(36.55, -17.67) * mm, "mid": v(37.43, -18.49) * mm, "end": v(37.68, -19.66) * mm});
            skLineSegment(sketch, "E155.MirrorCS", {"start": v(39.45, -15.08) * mm, "end": v(41.5, -15.03) * mm});
            skLineSegment(sketch, "E156.MirrorCS", {"start": v(41.5, -15.03) * mm, "end": v(42.7, -13.69) * mm});
            skLineSegment(sketch, "E157.MirrorCS", {"start": v(7.78, 2.12) * mm, "end": v(16.65, 2.48) * mm});
            skArc(sketch, "E158.MirrorCS", {"start": v(7.78, 2.12) * mm, "mid": v(7.36, 3.06) * mm, "end": v(7.73, 4.03) * mm});
            skLineSegment(sketch, "E159.MirrorCS", {"start": v(13.6, 5.62) * mm, "end": v(7.73, 4.03) * mm});
            skArc(sketch, "E160.MirrorCS", {"start": v(13.6, 5.62) * mm, "mid": v(23.73, 3.48) * mm, "end": v(33.1, -0.89) * mm});
            skArc(sketch, "E161.MirrorCS", {"start": v(31.41, 4.2) * mm, "mid": v(23.41, 5.83) * mm, "end": v(15.75, 8.65) * mm});
            skArc(sketch, "E162.MirrorCS", {"start": v(12.52, 8.56) * mm, "mid": v(14.13, 8.9) * mm, "end": v(15.75, 8.65) * mm});
            skArc(sketch, "E163.MirrorCS", {"start": v(12.52, 8.56) * mm, "mid": v(10.36, 6.98) * mm, "end": v(8, 5.73) * mm});
            skArc(sketch, "E164.MirrorCS", {"start": v(8, 5.73) * mm, "mid": v(7.32, 5.96) * mm, "end": v(7.16, 6.65) * mm});
            skArc(sketch, "E165.MirrorCS", {"start": v(38.32, 4.37) * mm, "mid": v(36, 1.46) * mm, "end": v(33.1, -0.89) * mm});
            skArc(sketch, "E166.MirrorCS", {"start": v(23.1, 41.4) * mm, "mid": v(33.21, 23.91) * mm, "end": v(38.32, 4.37) * mm});
            skArc(sketch, "E167.MirrorCS", {"start": v(23.1, 41.4) * mm, "mid": v(30.7, 24.24) * mm, "end": v(32.94, 5.6) * mm});
            skArc(sketch, "E168.MirrorCS", {"start": v(27.68, 12.07) * mm, "mid": v(26, 10.26) * mm, "end": v(23.97, 8.86) * mm});
            skArc(sketch, "E169.MirrorCS", {"start": v(9.8, 10.41) * mm, "mid": v(16.3, 10.92) * mm, "end": v(22.77, 10.15) * mm});
            skArc(sketch, "E170.MirrorCS", {"start": v(23.97, 8.86) * mm, "mid": v(23.3, 9.43) * mm, "end": v(22.77, 10.15) * mm});
            skArc(sketch, "E171.MirrorCS", {"start": v(7.16, 6.65) * mm, "mid": v(8.14, 8.77) * mm, "end": v(9.8, 10.41) * mm});
            skArc(sketch, "E172.MirrorCS", {"start": v(22.1, 12.74) * mm, "mid": v(15.56, 12.32) * mm, "end": v(9.07, 13.38) * mm});
            skArc(sketch, "E173.MirrorCS", {"start": v(8.13, 13.35) * mm, "mid": v(8.6, 13.51) * mm, "end": v(9.07, 13.38) * mm});
            skArc(sketch, "E174.MirrorCS", {"start": v(17.1, 41.25) * mm, "mid": v(21.12, 27.74) * mm, "end": v(22.68, 13.73) * mm});
            skArc(sketch, "E175.MirrorCS", {"start": v(17.1, 41.25) * mm, "mid": v(24.13, 27.3) * mm, "end": v(27.68, 12.07) * mm});
            skArc(sketch, "E176.MirrorCS", {"start": v(8.13, 13.35) * mm, "mid": v(7, 10.73) * mm, "end": v(4.82, 8.89) * mm});
            skArc(sketch, "E177.MirrorCS", {"start": v(1.55, 11.65) * mm, "mid": v(3, 10.92) * mm, "end": v(3.97, 9.6) * mm});
            skArc(sketch, "E178.MirrorCS", {"start": v(2.46, 9.57) * mm, "mid": v(1.86, 10.55) * mm, "end": v(1.55, 11.65) * mm});
            skArc(sketch, "E179.MirrorCS", {"start": v(0.58, 9.52) * mm, "mid": v(1.24, 8.9) * mm, "end": v(1.5, 8.03) * mm});
            skArc(sketch, "E180.MirrorCS", {"start": v(-0.12, 7.99) * mm, "mid": v(0.07, 8.83) * mm, "end": v(0.58, 9.52) * mm});
            skArc(sketch, "E181.MirrorCS", {"start": v(-0.12, 7.99) * mm, "mid": v(-0.43, 7.76) * mm, "end": v(-0.78, 7.6) * mm});
            skArc(sketch, "E182.MirrorCS", {"start": v(2.5, 8.05) * mm, "mid": v(2, 7.79) * mm, "end": v(1.5, 8.03) * mm});
            skArc(sketch, "E183.MirrorCS", {"start": v(4.82, 8.89) * mm, "mid": v(4.32, 9.16) * mm, "end": v(3.97, 9.6) * mm});
            skArc(sketch, "E184.MirrorCS", {"start": v(2.46, 9.57) * mm, "mid": v(2.67, 9.42) * mm, "end": v(2.75, 9.19) * mm});
            skArc(sketch, "E185.MirrorCS", {"start": v(2.75, 9.19) * mm, "mid": v(2.74, 8.6) * mm, "end": v(2.5, 8.05) * mm});
            skArc(sketch, "E186.MirrorCS", {"start": v(22.68, 13.73) * mm, "mid": v(22.55, 13.15) * mm, "end": v(22.1, 12.74) * mm});
            skArc(sketch, "E187.MirrorCS", {"start": v(32.94, 5.6) * mm, "mid": v(32.66, 4.37) * mm, "end": v(31.41, 4.2) * mm});
            skSolve(sketch);
        }
        {
            var Q1;
            Q1=makeQuery(id+"F3.imprint","IMPRINT",FACE,{"disambiguationData":[TD([[makeQuery(id+"F3.imprint","IMPRINT",EDGE,{"derivedFrom":sQuery(id+"F3.wireOp",EDGE,"E94")}),1.0]])]});
            var Q2;
            Q2=makeQuery(id+"F1.opExtrude","CAP_FACE",FACE,{"disambiguationData":[OSD([sQuery(id+"F0.wireOp",EDGE,"E0"),sQuery(id+"F0.wireOp",EDGE,"E1"),sQuery(id+"F0.wireOp",EDGE,"E2"),sQuery(id+"F0.wireOp",EDGE,"E3"),sQuery(id+"F0.wireOp",EDGE,"E4"),sQuery(id+"F0.wireOp",EDGE,"E5"),sQuery(id+"F0.wireOp",EDGE,"E6"),sQuery(id+"F0.wireOp",EDGE,"E7"),sQuery(id+"F0.wireOp",EDGE,"E8"),sQuery(id+"F0.wireOp",EDGE,"E9"),sQuery(id+"F0.wireOp",EDGE,"E10"),sQuery(id+"F0.wireOp",EDGE,"E11"),sQuery(id+"F0.wireOp",EDGE,"E12"),sQuery(id+"F0.wireOp",EDGE,"E13"),sQuery(id+"F0.wireOp",EDGE,"E14"),sQuery(id+"F0.wireOp",EDGE,"E15"),sQuery(id+"F0.wireOp",EDGE,"E16"),sQuery(id+"F0.wireOp",EDGE,"E17"),sQuery(id+"F0.wireOp",EDGE,"E18"),sQuery(id+"F0.wireOp",EDGE,"E19"),sQuery(id+"F0.wireOp",EDGE,"E20"),sQuery(id+"F0.wireOp",EDGE,"E21"),sQuery(id+"F0.wireOp",EDGE,"E22"),sQuery(id+"F0.wireOp",EDGE,"E23"),sQuery(id+"F0.wireOp",EDGE,"E24"),sQuery(id+"F0.wireOp",EDGE,"E25"),sQuery(id+"F0.wireOp",EDGE,"E26"),sQuery(id+"F0.wireOp",EDGE,"E27"),sQuery(id+"F0.wireOp",EDGE,"E28"),sQuery(id+"F0.wireOp",EDGE,"E29"),sQuery(id+"F0.wireOp",EDGE,"E30"),sQuery(id+"F0.wireOp",EDGE,"E31"),sQuery(id+"F0.wireOp",EDGE,"E32"),sQuery(id+"F0.wireOp",EDGE,"E33"),sQuery(id+"F0.wireOp",EDGE,"E34"),sQuery(id+"F0.wireOp",EDGE,"E35"),sQuery(id+"F0.wireOp",EDGE,"E36"),sQuery(id+"F0.wireOp",EDGE,"E37"),sQuery(id+"F0.wireOp",EDGE,"E38"),sQuery(id+"F0.wireOp",EDGE,"E39"),sQuery(id+"F0.wireOp",EDGE,"E40"),sQuery(id+"F0.wireOp",EDGE,"E41"),sQuery(id+"F0.wireOp",EDGE,"E42"),sQuery(id+"F0.wireOp",EDGE,"E43"),sQuery(id+"F0.wireOp",EDGE,"E44"),sQuery(id+"F0.wireOp",EDGE,"E45"),sQuery(id+"F0.wireOp",EDGE,"E47.MirrorCS"),sQuery(id+"F0.wireOp",EDGE,"E48.MirrorCS"),sQuery(id+"F0.wireOp",EDGE,"E49.MirrorCS"),sQuery(id+"F0.wireOp",EDGE,"E50.MirrorCS"),sQuery(id+"F0.wireOp",EDGE,"E51.MirrorCS"),sQuery(id+"F0.wireOp",EDGE,"E52.MirrorCS"),sQuery(id+"F0.wireOp",EDGE,"E53.MirrorCS"),sQuery(id+"F0.wireOp",EDGE,"E54.MirrorCS"),sQuery(id+"F0.wireOp",EDGE,"E55.MirrorCS"),sQuery(id+"F0.wireOp",EDGE,"E56.MirrorCS"),sQuery(id+"F0.wireOp",EDGE,"E57.MirrorCS"),sQuery(id+"F0.wireOp",EDGE,"E58.MirrorCS"),sQuery(id+"F0.wireOp",EDGE,"E59.MirrorCS"),sQuery(id+"F0.wireOp",EDGE,"E60.MirrorCS"),sQuery(id+"F0.wireOp",EDGE,"E61.MirrorCS"),sQuery(id+"F0.wireOp",EDGE,"E62.MirrorCS"),sQuery(id+"F0.wireOp",EDGE,"E63.MirrorCS"),sQuery(id+"F0.wireOp",EDGE,"E64.MirrorCS"),sQuery(id+"F0.wireOp",EDGE,"E65.MirrorCS"),sQuery(id+"F0.wireOp",EDGE,"E66.MirrorCS"),sQuery(id+"F0.wireOp",EDGE,"E67.MirrorCS"),sQuery(id+"F0.wireOp",EDGE,"E68.MirrorCS"),sQuery(id+"F0.wireOp",EDGE,"E69.MirrorCS"),sQuery(id+"F0.wireOp",EDGE,"E70.MirrorCS"),sQuery(id+"F0.wireOp",EDGE,"E71.MirrorCS"),sQuery(id+"F0.wireOp",EDGE,"E72.MirrorCS"),sQuery(id+"F0.wireOp",EDGE,"E73.MirrorCS"),sQuery(id+"F0.wireOp",EDGE,"E74.MirrorCS"),sQuery(id+"F0.wireOp",EDGE,"E75.MirrorCS"),sQuery(id+"F0.wireOp",EDGE,"E76.MirrorCS"),sQuery(id+"F0.wireOp",EDGE,"E77.MirrorCS"),sQuery(id+"F0.wireOp",EDGE,"E78.MirrorCS"),sQuery(id+"F0.wireOp",EDGE,"E79.MirrorCS"),sQuery(id+"F0.wireOp",EDGE,"E80.MirrorCS"),sQuery(id+"F0.wireOp",EDGE,"E81.MirrorCS"),sQuery(id+"F0.wireOp",EDGE,"E82.MirrorCS"),sQuery(id+"F0.wireOp",EDGE,"E83.MirrorCS"),sQuery(id+"F0.wireOp",EDGE,"E84.MirrorCS"),sQuery(id+"F0.wireOp",EDGE,"E85.MirrorCS"),sQuery(id+"F0.wireOp",EDGE,"E86.MirrorCS"),sQuery(id+"F0.wireOp",EDGE,"E88.MirrorCS"),sQuery(id+"F0.wireOp",EDGE,"E89.MirrorCS"),sQuery(id+"F0.wireOp",EDGE,"E90.MirrorCS"),sQuery(id+"F0.wireOp",EDGE,"E91.MirrorCS"),sQuery(id+"F0.wireOp",EDGE,"E92.MirrorCS"),sQuery(id+"F0.wireOp",EDGE,"E93.MirrorCS")])],"isStart":true});
            loft(context, id + "F4", {"operationType" : NewBodyOperationType.ADD, "sheetProfilesArray" : [{ "sheetProfileEntities" : qUnion([Q1]) }, { "sheetProfileEntities" : qUnion([Q2]) }]});
        }
    });
